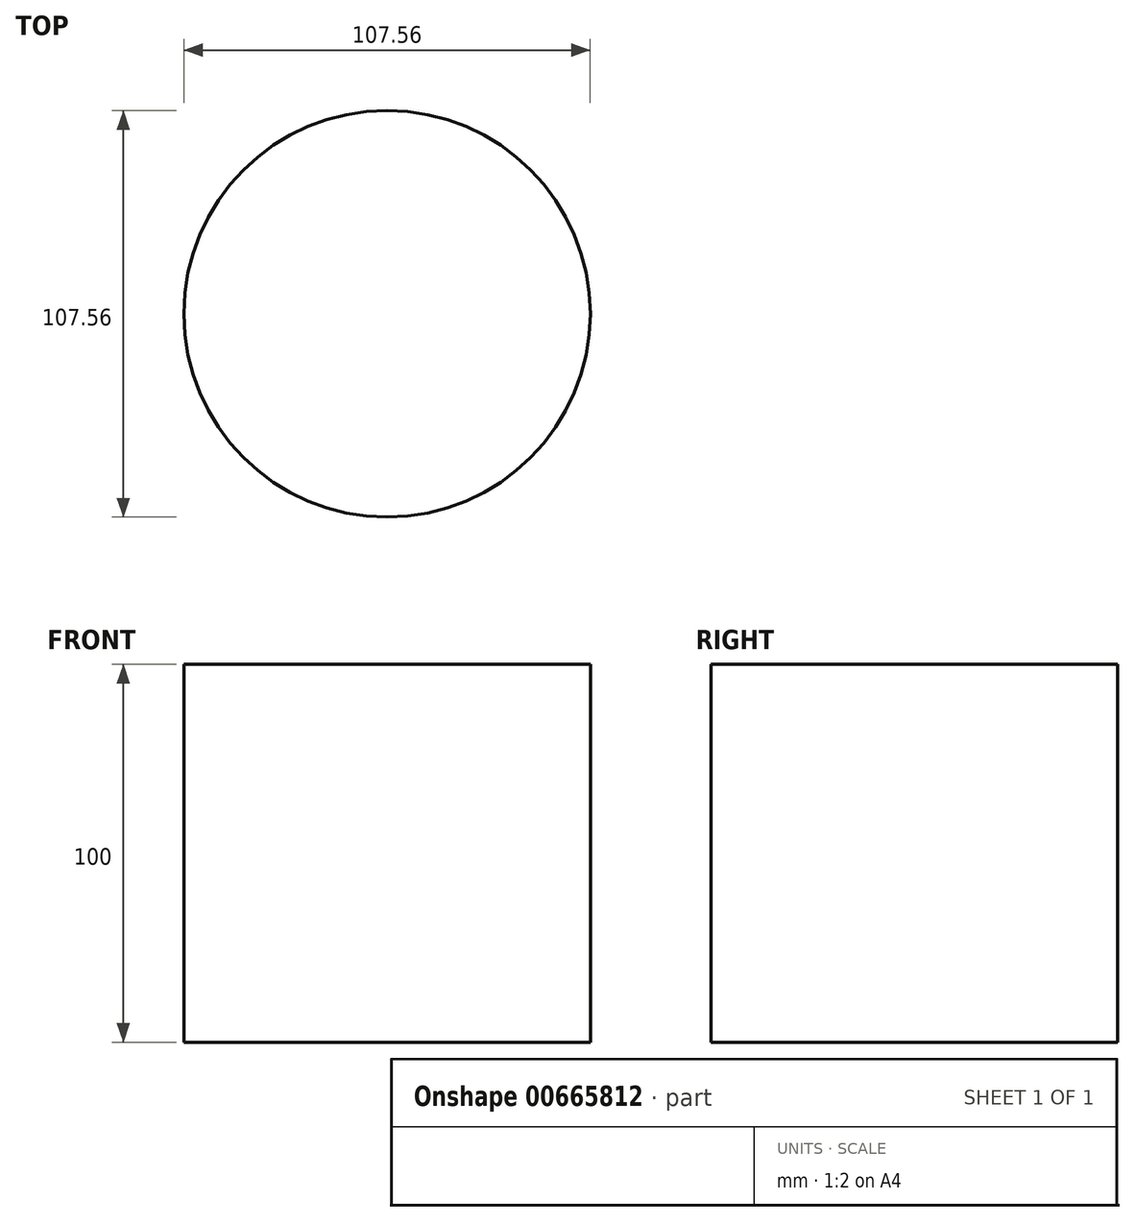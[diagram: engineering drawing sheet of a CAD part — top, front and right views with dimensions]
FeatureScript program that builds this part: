
annotation { "Feature Type Name" : "Feature", "Feature Type Description" : "" }
export const myFeature = defineFeature(function(context is Context, id is Id, definition is map)
    precondition{}
    {
        {
            var Q0;
            Q0=qCreatedBy(makeId("Top.planeOp"),FACE);
            var sketch = newSketch(context, id + "F0", { "sketchPlane" : qUnion([Q0])});
            skCircle(sketch, "E0", {"center": v(1.52, 0) * mm, "radius": 53.78 * mm});
            skSolve(sketch);
        }
        {
            var Q0;
            Q0 = qSketchRegion(id + "F0", true);
            extrude(context, id + "F1", {"entities" : qUnion([Q0]), "depth" : 100 * mm, "offsetDistance" : 25 * mm});
        }
    });
